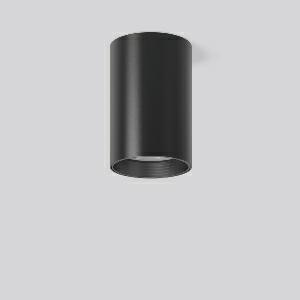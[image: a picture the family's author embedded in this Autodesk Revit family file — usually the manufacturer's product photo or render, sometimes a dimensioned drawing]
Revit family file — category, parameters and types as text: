
# Revit family: heledon_maxi_a_931227_003_1_76_e1eb
name_source: partatom
category: Lighting Fixtures
units: mm (PartAtom-declared; Revit-internal decimal feet)

## family parameters
Cut with Voids When Loaded = No
Host = Face
Light Source = No
Part Type = Normal
Room Calculation Point = No
Round Connector Dimension = Use Diameter
Shared = No

## types (1)
- HELEDON maxi A (1 x LED Modul 940, 3900 lm, 4000)
    Apparent Load = 35 VA
    Approval mark = CE
    CIE Flux Codes = 97 100 100 100 100
    Color Rendering = 92
    Color Temperature = 4000
    Default Elevation = 1800 mm
    Description = Series: HELEDON maxi
Cylindrical surface-mounted downlight. Housing: die-cast aluminium, powder-coated. Internal ceiling frame polycarbonate with bayonet mounting. Black plastic ring and recessed LED to prevent glare from the side. Optical assembly with lens made of plastic (polycarbonate) for the best homogeneous light distribution - can be changed without tools. Best colour rendering index Ra>90. Suitable for Ceiling mounting. Easy installation with a separate ceiling frame with bayonet mounting and plug connection. Driver integrated. Connected via plug-in connector. High quality converter without flickering and stroboscopic effect. The following accessories can be mounted without use of tools: interchangeable lenses, decorative glasses, honeycomb louvre, clear and frosted diffusers, white interchangeable plastic ring. 
Colour: deep black, matt (RAL 9005)
Diameter: 123 mm
Height: 183 mm
Lamp: LED
Socket: without socket
Colour temperature: 4000K
Colour rendering index (CRI): 92
System power: 35 W
Rated luminous flux: 3900 lm
Luminous efficiency: 111 lm/W
Control gear: Converter, dimmable, DALI
Protection class: I
Type of protection: IP 20
    Height = 183 mm
    Lamp = 1 x LED Modul 940
    Lamp Light Flux = 3900 lm
    Lamp count = 1
    Length = 123 mm
    Lifetime = 50000 h
    Luminous efficacy = 111 lm/W
    Manufacturer = RZB
    ModVariant = No
    Model = 931227.003.1.76
    Mounting Place = Ceiling
    Mounting Type = Surface mounted
    Number of Poles = 1
    OnlyDefault = Yes
    Power Factor = 1
    Product Name = HELEDON maxi A
    Product group = Surface mounted downlights
    ProductGroupID = 302
    Protection Class = Protection class I
    Protection Degree = IP 20
    RLX_Detail_Level = 1
    RLX_Emergency_Light_Flux = 0 lm
    RLX_Emergency_Type = 0
    RLX_Emergency_Type_DB = No
    RlxData = <blob elided: 97057 chars, md5=2926d63c>
    Socket = socket
    Standby Power = 0 W
    System Light Flux = 3900 lm
    System Power = 35 W
    Type Comments = Product without accessories
    Type Image = 931193.003.jpg
    URL = http://relux.com
    VarID = ---
    Voltage = 230 V
    Voltage Range = 220-240 V
    Weight = 0.00 kg
    Width = 0 mm  [stored 0 ft]

note: [stored X ft] marks values corroborated as IEEE doubles in the binary element streams (Revit-internal decimal feet)

## geometry (parser evidence)
native form markers: Blend x4, Sweep x10
no freeform markers — native parametric forms only
